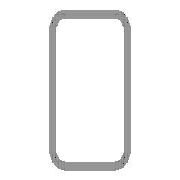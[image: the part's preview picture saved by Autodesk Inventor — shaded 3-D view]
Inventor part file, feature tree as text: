
AUTODESK INVENTOR PART (.ipt)
format: ipt  version: 2025 (Build 290162010, 162A)  size: 131,584 bytes
history: native  units: mm (DEFAULTED — no unit token found)
features: other x4, sketch x1, plane x1
ambient origin geometry x8: Origin, YZ Plane, XZ Plane, XY Plane, X Axis, Y Axis, Z Axis, Center Point
bodies: Solid1 (feature_tree), Body (feature_tree)
feature tree (6):
  parser-record x1  (decoder bookkeeping rows leaked as tree rows — omitted from the tree; the rows remain in map.json)
  other  "Driven Length"
  other  "Start Plane"
  other  "End Plane"
  sketch  "Sketch3"  dims[d3=780.0mm d4=0.0mm d7=6.0mm d9=40.0mm d11=80.0mm d12=3.0mm d13=-0.0mm d14=780.0mm d15=20.0mm d16=40.0mm d17=90.0deg d18=780.0mm]
  plane  "Work Plane3"
